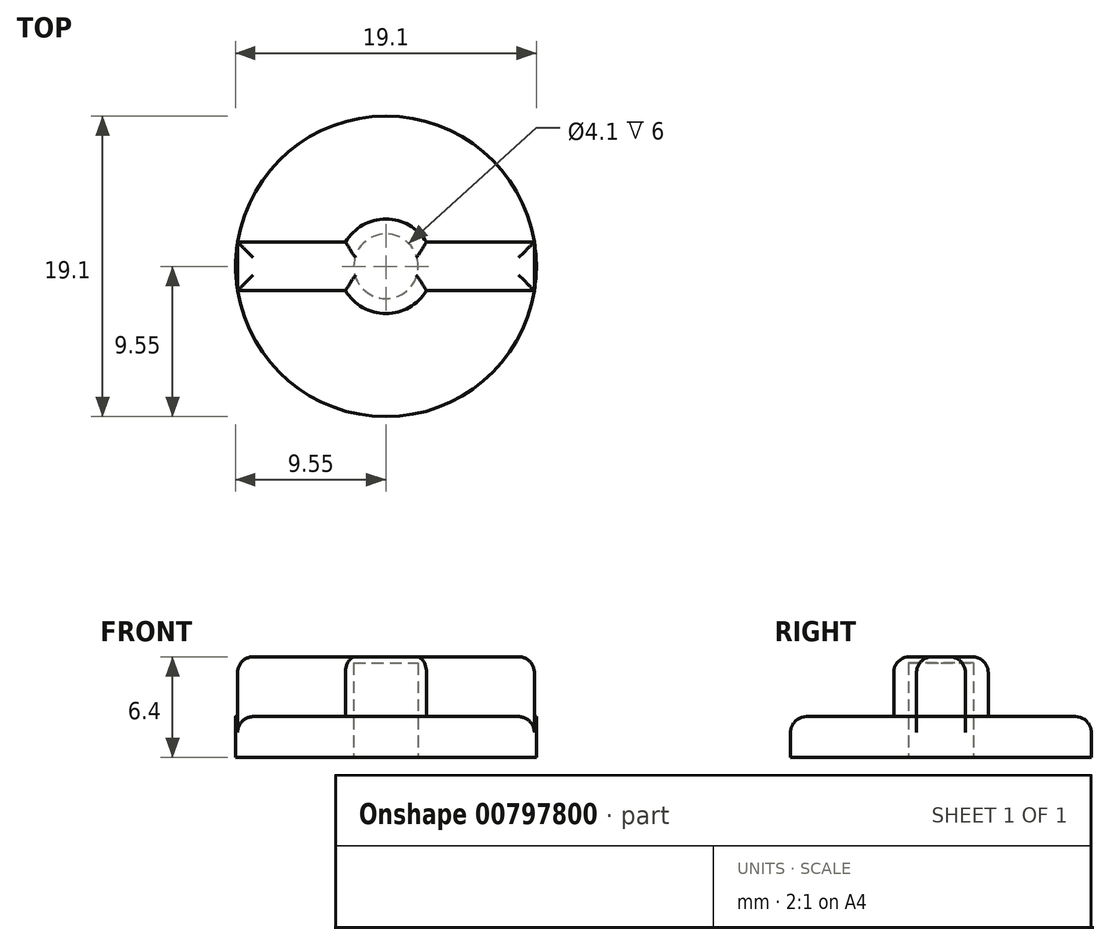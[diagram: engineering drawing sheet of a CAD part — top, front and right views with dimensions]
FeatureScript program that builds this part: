
annotation { "Feature Type Name" : "Feature", "Feature Type Description" : "" }
export const myFeature = defineFeature(function(context is Context, id is Id, definition is map)
    precondition{}
    {
        {
            var Q0;
            Q0=qCreatedBy(makeId("Top.planeOp"),FACE);
            var sketch = newSketch(context, id + "F0", { "sketchPlane" : qUnion([Q0])});
            skCircle(sketch, "E0", {"center": v(0, 0) * mm, "radius": 9.55 * mm});
            skLineSegment(sketch, "E1.bottom", {"start": v(9.42, 1.55) * mm, "end": v(-9.42, 1.55) * mm});
            skLineSegment(sketch, "E1.top", {"start": v(9.42, -1.55) * mm, "end": v(-9.42, -1.55) * mm});
            skLineSegment(sketch, "E1.left", {"start": v(9.42, 1.55) * mm, "end": v(9.42, -1.55) * mm});
            skLineSegment(sketch, "E1.right", {"start": v(-9.42, 1.55) * mm, "end": v(-9.42, -1.55) * mm});
            skCircle(sketch, "E2", {"center": v(0, 0) * mm, "radius": 3 * mm});
            skCircle(sketch, "E3", {"center": v(0, 0) * mm, "radius": 2.05 * mm});
            skSolve(sketch);
        }
        {
            var Q0;
            {var subQ0=sQuery(id+"F0.wireOp",EDGE,"E1.left");Q0=makeQuery(id+"F0.imprint","IMPRINT",FACE,{"disambiguationData":[TD([[makeQuery(id+"F0.imprint","IMPRINT",EDGE,{"derivedFrom":subQ0}),-1.0]])]});}
            var Q1;
            {var subQ0=sQuery(id+"F0.wireOp",EDGE,"E2");var subQ1=sQuery(id+"F0.wireOp",EDGE,"E1.bottom");var subQ2=makeQuery(id+"F0.imprint","INTERSECT",VERTEX,{"disambiguationData":[OD(0.0)],"derivedFrom":[subQ1,subQ0]});Q1=makeQuery(id+"F0.imprint","IMPRINT",FACE,{"disambiguationData":[TD([[makeQuery(id+"F0.imprint","IMPRINT",EDGE,{"disambiguationData":[TD([[subQ2,-1.0]])],"derivedFrom":subQ1}),1.0]])]});}
            var Q2;
            {var subQ0=sQuery(id+"F0.wireOp",EDGE,"E2");var subQ1=sQuery(id+"F0.wireOp",EDGE,"E1.bottom");var subQ2=makeQuery(id+"F0.imprint","INTERSECT",VERTEX,{"disambiguationData":[OD(0.0)],"derivedFrom":[subQ1,subQ0]});Q2=makeQuery(id+"F0.imprint","IMPRINT",FACE,{"disambiguationData":[TD([[makeQuery(id+"F0.imprint","IMPRINT",EDGE,{"disambiguationData":[TD([[subQ2,-1.0]])],"derivedFrom":subQ1}),-1.0]])]});}
            var Q3;
            {var subQ0=sQuery(id+"F0.wireOp",EDGE,"E2");var subQ1=sQuery(id+"F0.wireOp",EDGE,"E1.top");var subQ2=makeQuery(id+"F0.imprint","INTERSECT",VERTEX,{"disambiguationData":[OD(0.0)],"derivedFrom":[subQ1,subQ0]});Q3=makeQuery(id+"F0.imprint","IMPRINT",FACE,{"disambiguationData":[TD([[makeQuery(id+"F0.imprint","IMPRINT",EDGE,{"disambiguationData":[TD([[subQ2,-1.0]])],"derivedFrom":subQ1}),1.0]])]});}
            var Q4;
            {var subQ0=sQuery(id+"F0.wireOp",EDGE,"E1.right");Q4=makeQuery(id+"F0.imprint","IMPRINT",FACE,{"disambiguationData":[TD([[makeQuery(id+"F0.imprint","IMPRINT",EDGE,{"derivedFrom":subQ0}),1.0]])]});}
            var Q5;
            {var subQ0=sQuery(id+"F0.wireOp",EDGE,"E3");var subQ1=sQuery(id+"F0.wireOp",EDGE,"E1.bottom");var subQ2=makeQuery(id+"F0.imprint","INTERSECT",VERTEX,{"disambiguationData":[OD(1.0)],"derivedFrom":[subQ1,subQ0]});Q5=makeQuery(id+"F0.imprint","IMPRINT",FACE,{"disambiguationData":[TD([[makeQuery(id+"F0.imprint","IMPRINT",EDGE,{"disambiguationData":[TD([[subQ2,-1.0]])],"derivedFrom":subQ1}),1.0]])]});}
            var Q6;
            {var subQ0=sQuery(id+"F0.wireOp",EDGE,"E3");var subQ1=sQuery(id+"F0.wireOp",EDGE,"E1.bottom");var subQ2=makeQuery(id+"F0.imprint","INTERSECT",VERTEX,{"disambiguationData":[OD(0.0)],"derivedFrom":[subQ1,subQ0]});Q6=makeQuery(id+"F0.imprint","IMPRINT",FACE,{"disambiguationData":[TD([[makeQuery(id+"F0.imprint","IMPRINT",EDGE,{"disambiguationData":[TD([[subQ2,-1.0]])],"derivedFrom":subQ1}),1.0]])]});}
            var Q7;
            {var subQ0=sQuery(id+"F0.wireOp",EDGE,"E3");var subQ1=sQuery(id+"F0.wireOp",EDGE,"E1.bottom");var subQ2=makeQuery(id+"F0.imprint","INTERSECT",VERTEX,{"disambiguationData":[OD(0.0)],"derivedFrom":[subQ1,subQ0]});Q7=makeQuery(id+"F0.imprint","IMPRINT",FACE,{"disambiguationData":[TD([[makeQuery(id+"F0.imprint","IMPRINT",EDGE,{"disambiguationData":[TD([[subQ2,-1.0]])],"derivedFrom":subQ1}),-1.0]])]});}
            var Q8;
            {var subQ0=sQuery(id+"F0.wireOp",EDGE,"E3");var subQ1=sQuery(id+"F0.wireOp",EDGE,"E1.top");var subQ2=makeQuery(id+"F0.imprint","INTERSECT",VERTEX,{"disambiguationData":[OD(0.0)],"derivedFrom":[subQ1,subQ0]});Q8=makeQuery(id+"F0.imprint","IMPRINT",FACE,{"disambiguationData":[TD([[makeQuery(id+"F0.imprint","IMPRINT",EDGE,{"disambiguationData":[TD([[subQ2,-1.0]])],"derivedFrom":subQ1}),1.0]])]});}
            extrude(context, id + "F1", {"entities" : qUnion([Q0, Q1, Q2, Q3, Q4, Q5, Q6, Q7, Q8]), "depth" : 6.4 * mm, "offsetDistance" : 25 * mm});
        }
        {
            var Q0;
            Q0 = qSketchRegion(id + "F0", true);
            extrude(context, id + "F2", {"entities" : qUnion([Q0]), "operationType" : NewBodyOperationType.ADD, "depth" : 2.6 * mm, "offsetDistance" : 25 * mm});
        }
        {
            var Q0;
            {var subQ0=sQuery(id+"F0.wireOp",EDGE,"E2");Q0=makeQuery(id+"F2.boolean.opBoolean","MERGE",FACE,{"derivedFrom":[makeQuery(id+"F1.opExtrude","CAP_FACE",FACE,{"disambiguationData":[OSD([sQuery(id+"F0.wireOp",EDGE,"E1.bottom"),sQuery(id+"F0.wireOp",EDGE,"E1.top"),sQuery(id+"F0.wireOp",EDGE,"E1.left"),sQuery(id+"F0.wireOp",EDGE,"E1.right"),subQ0])],"isStart":true}),makeQuery(id+"F2.opExtrude","CAP_FACE",FACE,{"disambiguationData":[OSD([sQuery(id+"F0.wireOp",EDGE,"E0"),subQ0])],"isStart":true})]});}
            var sketch = newSketch(context, id + "F3", { "sketchPlane" : qUnion([Q0])});
            skCircle(sketch, "E4", {"center": v(0, 0) * mm, "radius": 2.05 * mm});
            skSolve(sketch);
        }
        {
            var Q0;
            Q0=makeQuery(id+"F3.imprint","IMPRINT",FACE,{"disambiguationData":[TD([[makeQuery(id+"F3.imprint","IMPRINT",EDGE,{"derivedFrom":sQuery(id+"F3.wireOp",EDGE,"E4")}),1.0]])]});
            extrude(context, id + "F4", {"entities" : qUnion([Q0]), "operationType" : NewBodyOperationType.REMOVE, "oppositeDirection" : true, "depth" : 6 * mm, "offsetDistance" : 25 * mm});
        }
        {
            var Q0;
            {var subQ0=sQuery(id+"F0.wireOp",EDGE,"E1.bottom");Q0=makeQuery(id+"F1.opExtrude","CAP_EDGE",EDGE,{"disambiguationData":[OSD([subQ0]),TDD([makeQuery(id+"F0.imprint","IMPRINT",EDGE,{"disambiguationData":[TD([[makeQuery(id+"F0.imprint","INTERSECT",VERTEX,{"disambiguationData":[OD(0.0)],"derivedFrom":[subQ0,sQuery(id+"F0.wireOp",EDGE,"E2")]}),1.0]])],"derivedFrom":subQ0})])],"isStart":false});}
            var Q1;
            {var subQ0=sQuery(id+"F0.wireOp",EDGE,"E1.top");Q1=makeQuery(id+"F1.opExtrude","CAP_EDGE",EDGE,{"disambiguationData":[OSD([subQ0]),TDD([makeQuery(id+"F0.imprint","IMPRINT",EDGE,{"disambiguationData":[TD([[makeQuery(id+"F0.imprint","INTERSECT",VERTEX,{"disambiguationData":[OD(1.0)],"derivedFrom":[subQ0,sQuery(id+"F0.wireOp",EDGE,"E2")]}),-1.0]])],"derivedFrom":subQ0})])],"isStart":false});}
            var Q2;
            {var subQ0=sQuery(id+"F0.wireOp",EDGE,"E2");var subQ1=sQuery(id+"F0.wireOp",EDGE,"E1.bottom");Q2=makeQuery(id+"F1.opExtrude","CAP_EDGE",EDGE,{"disambiguationData":[OSD([subQ0]),TDD([makeQuery(id+"F0.imprint","IMPRINT",EDGE,{"disambiguationData":[TD([[makeQuery(id+"F0.imprint","INTERSECT",VERTEX,{"disambiguationData":[OD(0.0)],"derivedFrom":[subQ1,subQ0]}),-1.0]])],"derivedFrom":subQ0})])],"isStart":false});}
            var Q3;
            {var subQ0=sQuery(id+"F0.wireOp",EDGE,"E2");var subQ1=sQuery(id+"F0.wireOp",EDGE,"E1.top");Q3=makeQuery(id+"F1.opExtrude","CAP_EDGE",EDGE,{"disambiguationData":[OSD([subQ0]),TDD([makeQuery(id+"F0.imprint","IMPRINT",EDGE,{"disambiguationData":[TD([[makeQuery(id+"F0.imprint","INTERSECT",VERTEX,{"disambiguationData":[OD(0.0)],"derivedFrom":[subQ1,subQ0]}),1.0]])],"derivedFrom":subQ0})])],"isStart":false});}
            var Q4;
            {var subQ0=sQuery(id+"F0.wireOp",EDGE,"E1.right");var subQ1=sQuery(id+"F0.wireOp",EDGE,"E1.left");var subQ2=sQuery(id+"F0.wireOp",EDGE,"E2");var subQ3=sQuery(id+"F0.wireOp",EDGE,"E0");var subQ4=sQuery(id+"F0.wireOp",EDGE,"E1.bottom");Q4=makeQuery(id+"F2.boolean.opBoolean","SPLIT",EDGE,{"disambiguationData":[TD([makeQuery(id+"F1.opExtrude","SWEPT_FACE",FACE,{"disambiguationData":[OSD([subQ4]),TDD([makeQuery(id+"F0.imprint","IMPRINT",EDGE,{"disambiguationData":[TD([[makeQuery(id+"F0.imprint","INTERSECT",VERTEX,{"disambiguationData":[OD(0.0)],"derivedFrom":[subQ4,subQ2]}),1.0]])],"derivedFrom":subQ4})])]}),makeQuery(id+"F1.opExtrude","SWEPT_FACE",FACE,{"disambiguationData":[OSD([subQ4]),TDD([makeQuery(id+"F0.imprint","IMPRINT",EDGE,{"disambiguationData":[TD([[makeQuery(id+"F0.imprint","INTERSECT",VERTEX,{"disambiguationData":[OD(1.0)],"derivedFrom":[subQ4,subQ2]}),-1.0]])],"derivedFrom":subQ4})])]}),makeQuery(id+"F1.opExtrude","SWEPT_FACE",FACE,{"disambiguationData":[OSD([subQ1])]}),makeQuery(id+"F1.opExtrude","SWEPT_FACE",FACE,{"disambiguationData":[OSD([subQ0])]}),makeQuery(id+"F2.opExtrude","SWEPT_FACE",FACE,{"disambiguationData":[OSD([subQ3])]}),makeQuery(id+"F2.opExtrude","CAP_FACE",FACE,{"disambiguationData":[OSD([subQ3,subQ2])],"isStart":false})])],"derivedFrom":makeQuery(id+"F2.opExtrude","CAP_EDGE",EDGE,{"disambiguationData":[OSD([subQ3])],"isStart":false})});}
            var Q5;
            {var subQ0=sQuery(id+"F0.wireOp",EDGE,"E1.right");var subQ1=sQuery(id+"F0.wireOp",EDGE,"E1.left");var subQ2=sQuery(id+"F0.wireOp",EDGE,"E2");var subQ3=sQuery(id+"F0.wireOp",EDGE,"E0");var subQ4=sQuery(id+"F0.wireOp",EDGE,"E1.top");Q5=makeQuery(id+"F2.boolean.opBoolean","SPLIT",EDGE,{"disambiguationData":[TD([makeQuery(id+"F1.opExtrude","SWEPT_FACE",FACE,{"disambiguationData":[OSD([subQ4]),TDD([makeQuery(id+"F0.imprint","IMPRINT",EDGE,{"disambiguationData":[TD([[makeQuery(id+"F0.imprint","INTERSECT",VERTEX,{"disambiguationData":[OD(0.0)],"derivedFrom":[subQ4,subQ2]}),1.0]])],"derivedFrom":subQ4})])]}),makeQuery(id+"F1.opExtrude","SWEPT_FACE",FACE,{"disambiguationData":[OSD([subQ4]),TDD([makeQuery(id+"F0.imprint","IMPRINT",EDGE,{"disambiguationData":[TD([[makeQuery(id+"F0.imprint","INTERSECT",VERTEX,{"disambiguationData":[OD(1.0)],"derivedFrom":[subQ4,subQ2]}),-1.0]])],"derivedFrom":subQ4})])]}),makeQuery(id+"F1.opExtrude","SWEPT_FACE",FACE,{"disambiguationData":[OSD([subQ1])]}),makeQuery(id+"F1.opExtrude","SWEPT_FACE",FACE,{"disambiguationData":[OSD([subQ0])]}),makeQuery(id+"F2.opExtrude","SWEPT_FACE",FACE,{"disambiguationData":[OSD([subQ3])]}),makeQuery(id+"F2.opExtrude","CAP_FACE",FACE,{"disambiguationData":[OSD([subQ3,subQ2])],"isStart":false})])],"derivedFrom":makeQuery(id+"F2.opExtrude","CAP_EDGE",EDGE,{"disambiguationData":[OSD([subQ3])],"isStart":false})});}
            var Q6;
            Q6=makeQuery(id+"F1.opExtrude","CAP_EDGE",EDGE,{"disambiguationData":[OSD([sQuery(id+"F0.wireOp",EDGE,"E1.left")])],"isStart":false});
            var Q7;
            Q7=makeQuery(id+"F1.opExtrude","CAP_EDGE",EDGE,{"disambiguationData":[OSD([sQuery(id+"F0.wireOp",EDGE,"E1.right")])],"isStart":false});
            var Q8;
            {var subQ0=sQuery(id+"F0.wireOp",EDGE,"E1.top");Q8=makeQuery(id+"F1.opExtrude","CAP_EDGE",EDGE,{"disambiguationData":[OSD([subQ0]),TDD([makeQuery(id+"F0.imprint","IMPRINT",EDGE,{"disambiguationData":[TD([[makeQuery(id+"F0.imprint","INTERSECT",VERTEX,{"disambiguationData":[OD(0.0)],"derivedFrom":[subQ0,sQuery(id+"F0.wireOp",EDGE,"E2")]}),1.0]])],"derivedFrom":subQ0})])],"isStart":false});}
            var Q9;
            {var subQ0=sQuery(id+"F0.wireOp",EDGE,"E1.bottom");Q9=makeQuery(id+"F1.opExtrude","CAP_EDGE",EDGE,{"disambiguationData":[OSD([subQ0]),TDD([makeQuery(id+"F0.imprint","IMPRINT",EDGE,{"disambiguationData":[TD([[makeQuery(id+"F0.imprint","INTERSECT",VERTEX,{"disambiguationData":[OD(1.0)],"derivedFrom":[subQ0,sQuery(id+"F0.wireOp",EDGE,"E2")]}),-1.0]])],"derivedFrom":subQ0})])],"isStart":false});}
            fillet(context, id + "F5", {"entities" : qUnion([Q0, Q1, Q2, Q3, Q4, Q5, Q6, Q7, Q8, Q9]), "radius" : 1 * mm, "tangentPropagation" : true, "allowEdgeOverflow" : false});
        }
    });
